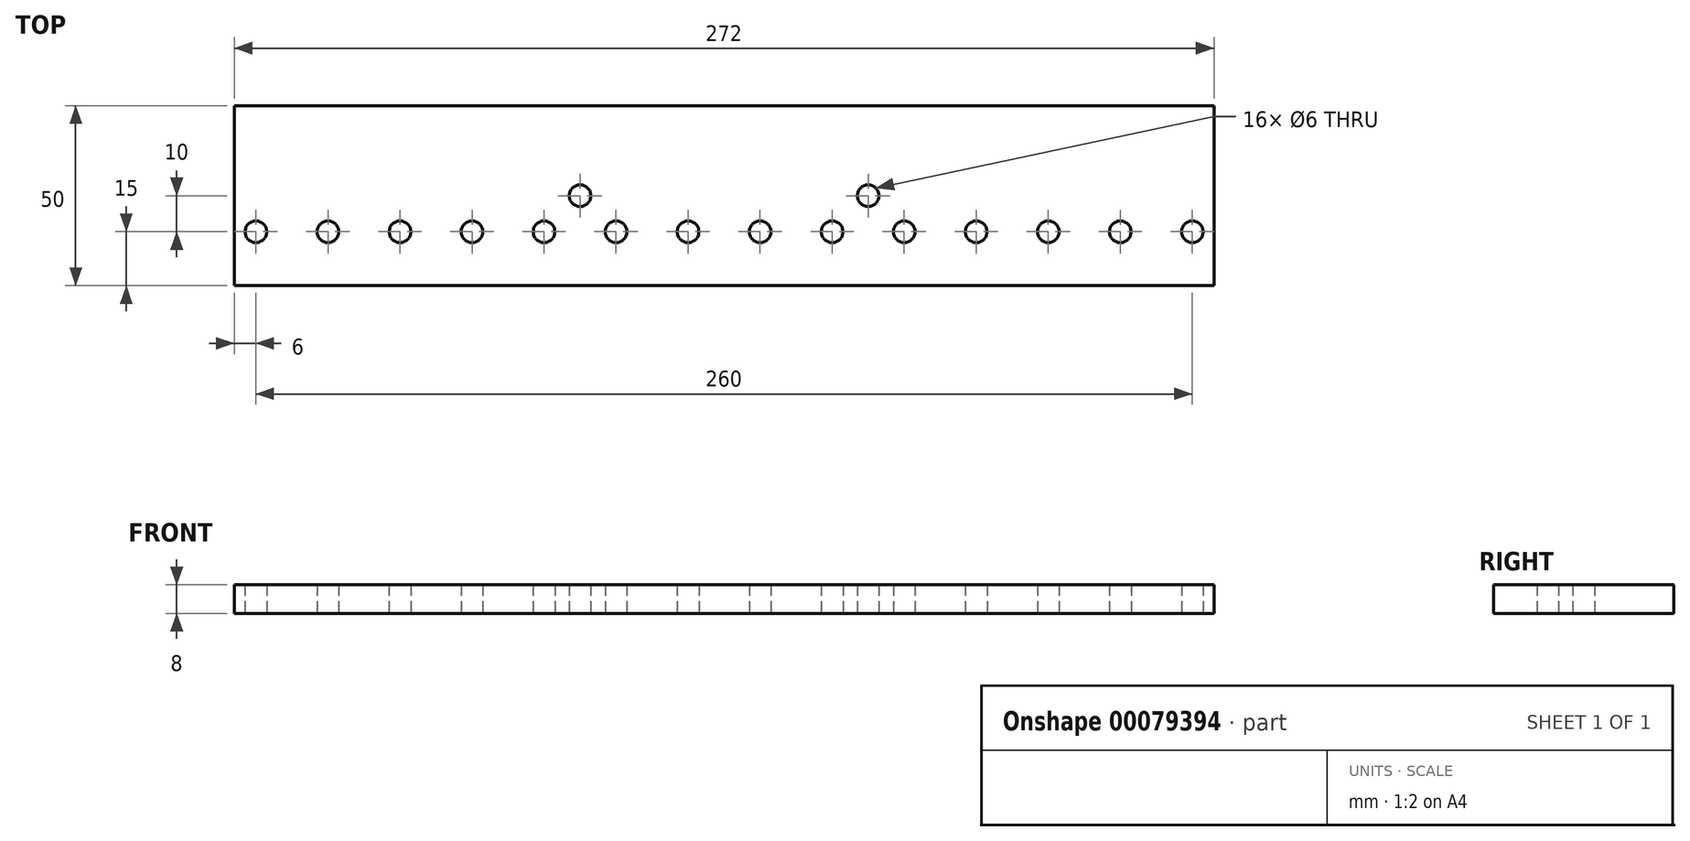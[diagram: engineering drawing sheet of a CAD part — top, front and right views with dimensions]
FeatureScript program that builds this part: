
annotation { "Feature Type Name" : "Feature", "Feature Type Description" : "" }
export const myFeature = defineFeature(function(context is Context, id is Id, definition is map)
    precondition{}
    {
        {
            var Q0;
            Q0=qCreatedBy(makeId("Top.planeOp"),FACE);
            var sketch = newSketch(context, id + "F0", { "sketchPlane" : qUnion([Q0])});
            skLineSegment(sketch, "E0.bottom", {"start": v(-136, 25) * mm, "end": v(136, 25) * mm});
            skLineSegment(sketch, "E0.top", {"start": v(-136, -25) * mm, "end": v(136, -25) * mm});
            skLineSegment(sketch, "E0.left", {"start": v(-136, 25) * mm, "end": v(-136, -25) * mm});
            skLineSegment(sketch, "E0.right", {"start": v(136, 25) * mm, "end": v(136, -25) * mm});
            skPoint(sketch, "E0.middle", {"position": v(0, 0) * mm});
            skPoint(sketch, "E1.endSnap0", {"position": v(0, -25) * mm});
            skCircle(sketch, "E2", {"center": v(-10, -10) * mm, "radius": 3 * mm});
            skCircle(sketch, "E3", {"center": v(10, -10) * mm, "radius": 3 * mm});
            skCircle(sketch, "E4.1.0.0", {"center": v(30, -10) * mm, "radius": 3 * mm});
            skCircle(sketch, "E4.2.0.0", {"center": v(50, -10) * mm, "radius": 3 * mm});
            skCircle(sketch, "E4.3.0.0", {"center": v(70, -10) * mm, "radius": 3 * mm});
            skCircle(sketch, "E4.4.0.0", {"center": v(90, -10) * mm, "radius": 3 * mm});
            skCircle(sketch, "E4.5.0.0", {"center": v(110, -10) * mm, "radius": 3 * mm});
            skCircle(sketch, "E4.6.0.0", {"center": v(130, -10) * mm, "radius": 3 * mm});
            skCircle(sketch, "E5.1.0.0", {"center": v(-30, -10) * mm, "radius": 3 * mm});
            skCircle(sketch, "E5.2.0.0", {"center": v(-50, -10) * mm, "radius": 3 * mm});
            skCircle(sketch, "E5.3.0.0", {"center": v(-70, -10) * mm, "radius": 3 * mm});
            skCircle(sketch, "E5.4.0.0", {"center": v(-90, -10) * mm, "radius": 3 * mm});
            skCircle(sketch, "E5.5.0.0", {"center": v(-110, -10) * mm, "radius": 3 * mm});
            skCircle(sketch, "E5.6.0.0", {"center": v(-130, -10) * mm, "radius": 3 * mm});
            skCircle(sketch, "E6", {"center": v(40, 0) * mm, "radius": 3 * mm});
            skCircle(sketch, "E7", {"center": v(-40, 0) * mm, "radius": 3 * mm});
            skSolve(sketch);
        }
        {
            var Q0;
            Q0=makeQuery(id+"F0.imprint","IMPRINT",FACE,{"disambiguationData":[TD([[makeQuery(id+"F0.imprint","IMPRINT",EDGE,{"derivedFrom":sQuery(id+"F0.wireOp",EDGE,"E0.bottom")}),-1.0]])]});
            extrude(context, id + "F1", {"entities" : qUnion([Q0]), "depth" : 8 * mm});
        }
    });
